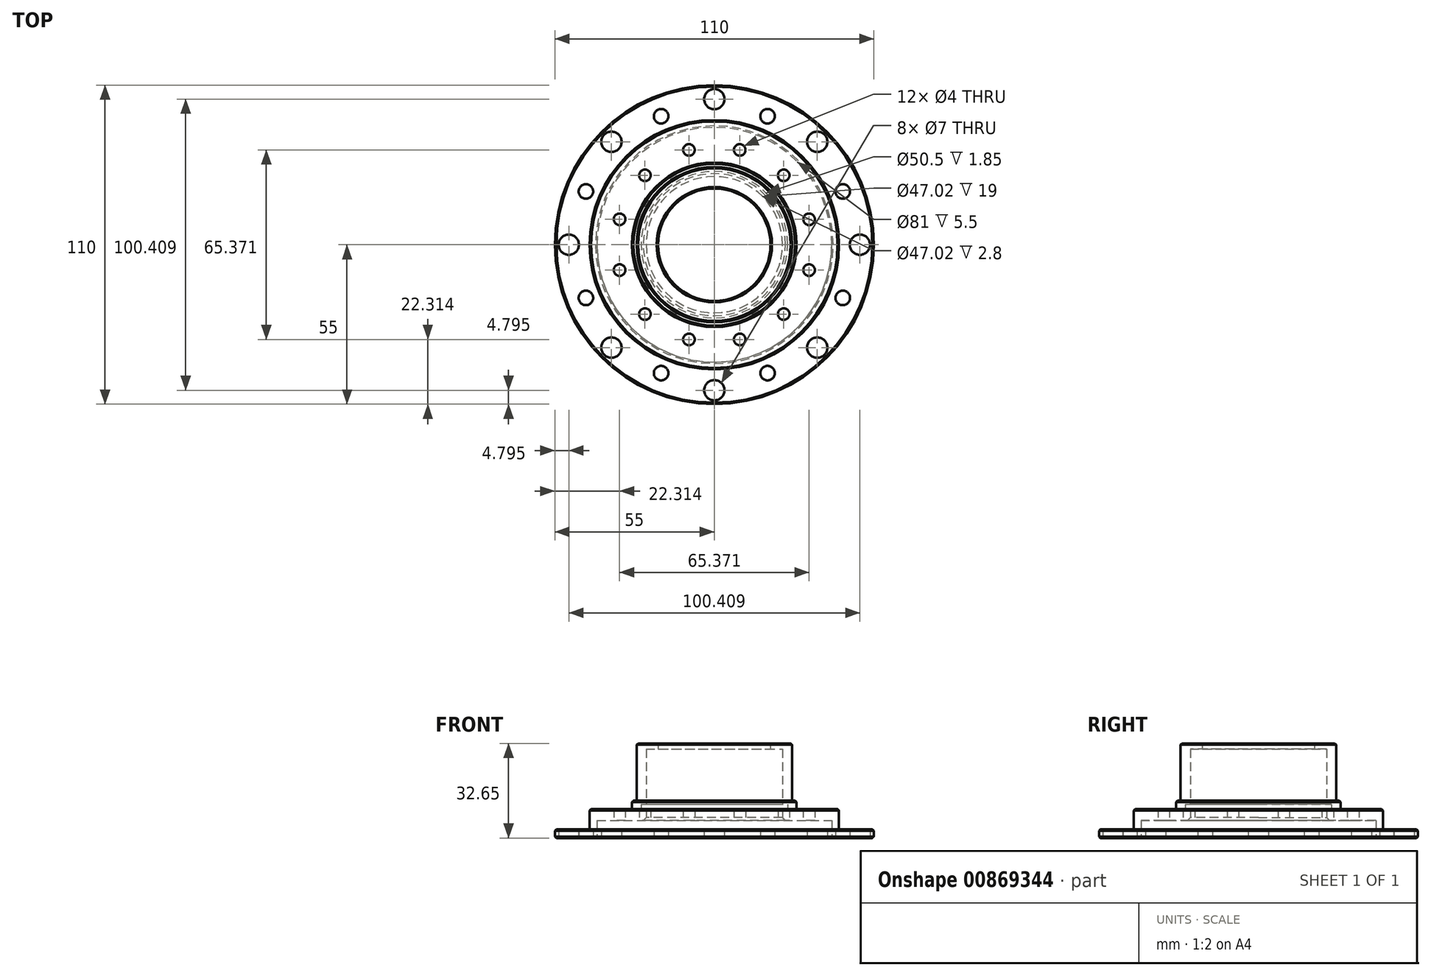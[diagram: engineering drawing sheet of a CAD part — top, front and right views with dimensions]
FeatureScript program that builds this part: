
annotation { "Feature Type Name" : "Feature", "Feature Type Description" : "" }
export const myFeature = defineFeature(function(context is Context, id is Id, definition is map)
    precondition{}
    {
        {
            var Q0;
            Q0=qCreatedBy(makeId("Front.planeOp"),FACE);
            var sketch = newSketch(context, id + "F0", { "sketchPlane" : qUnion([Q0])});
            skLineSegment(sketch, "E0", {"start": v(-40.5, 0) * mm, "end": v(-55, 0) * mm, "construction": true});
            skLineSegment(sketch, "E1", {"start": v(-55, 0) * mm, "end": v(-40.5, 0) * mm});
            skLineSegment(sketch, "E2", {"start": v(-40.5, 0) * mm, "end": v(-40.5, 6) * mm});
            skLineSegment(sketch, "E3", {"start": v(-55, 0) * mm, "end": v(-55, 3) * mm});
            skLineSegment(sketch, "E4", {"start": v(-55, 3) * mm, "end": v(-43, 3) * mm, "construction": true});
            skPoint(sketch, "E5", {"position": v(-43, 3) * mm});
            skLineSegment(sketch, "E6", {"start": v(-55, 3) * mm, "end": v(-43, 3) * mm});
            skLineSegment(sketch, "E7", {"start": v(-43, 3) * mm, "end": v(-43, 10) * mm});
            skLineSegment(sketch, "E8", {"start": v(-43, 10) * mm, "end": v(-28.39, 10) * mm});
            skPoint(sketch, "E9.orphan", {"position": v(0, 3) * mm});
            skPoint(sketch, "E10.orphan", {"position": v(0, 0) * mm});
            skPoint(sketch, "E11.end.orphan", {"position": v(0, 6) * mm});
            skPoint(sketch, "E11.start.orphan", {"position": v(0, 10) * mm});
            skLineSegment(sketch, "E12", {"start": v(-40.5, 6) * mm, "end": v(-23.51, 6) * mm});
            skLineSegment(sketch, "E13", {"start": v(-23.51, 9.8) * mm, "end": v(-25.25, 9.8) * mm});
            skLineSegment(sketch, "E14", {"start": v(-25.25, 9.8) * mm, "end": v(-25.25, 11.65) * mm});
            skLineSegment(sketch, "E15", {"start": v(-25.25, 11.65) * mm, "end": v(-23.51, 11.65) * mm});
            skLineSegment(sketch, "E16", {"start": v(-26.81, 12.92) * mm, "end": v(-26.81, 32.65) * mm});
            skLineSegment(sketch, "E17", {"start": v(-26.81, 32.65) * mm, "end": v(-19.38, 32.65) * mm});
            skLineSegment(sketch, "E18", {"start": v(-19.38, 32.65) * mm, "end": v(-19.38, 30.65) * mm});
            skLineSegment(sketch, "E19", {"start": v(-19.38, 30.65) * mm, "end": v(-23.51, 30.65) * mm});
            skLineSegment(sketch, "E20", {"start": v(-19.38, 30.65) * mm, "end": v(0, 30.65) * mm, "construction": true});
            skLineSegment(sketch, "E21", {"start": v(0, 30.65) * mm, "end": v(0, 32.65) * mm, "construction": true});
            skLineSegment(sketch, "E22", {"start": v(0, 32.65) * mm, "end": v(-19.38, 32.65) * mm, "construction": true});
            skLineSegment(sketch, "E23", {"start": v(-23.51, 9.8) * mm, "end": v(-23.51, 6) * mm});
            skLineSegment(sketch, "E24", {"start": v(-23.51, 11.65) * mm, "end": v(-23.51, 30.65) * mm});
            skLineSegment(sketch, "E25", {"start": v(-26.81, 12.92) * mm, "end": v(-28.39, 12.92) * mm});
            skLineSegment(sketch, "E26", {"start": v(-28.39, 12.92) * mm, "end": v(-28.39, 10) * mm});
            skPoint(sketch, "E27.orphan", {"position": v(-26.81, 10) * mm});
            skSolve(sketch);
        }
        {
            var Q0;
            Q0=makeQuery(id+"F0.imprint","IMPRINT",FACE,{"disambiguationData":[TD([[makeQuery(id+"F0.imprint","IMPRINT",EDGE,{"derivedFrom":sQuery(id+"F0.wireOp",EDGE,"E1")}),1.0]])]});
            var Q1;
            Q1=sQuery(id+"F0.wireOp",EDGE,"E21");
            revolve(context, id + "F1", {"surfaceOperationType" : NewSurfaceOperationType.NEW, "entities" : qUnion([Q0]), "axis" : qUnion([Q1]), "revolveType" : RevolveType.FULL});
        }
        {
            var Q0;
            Q0=qCreatedBy(makeId("Top.planeOp"),FACE);
            var sketch = newSketch(context, id + "F2", { "sketchPlane" : qUnion([Q0])});
            skCircle(sketch, "E28.cCircle", {"center": v(0, 0) * mm, "radius": 35.5 * mm, "construction": true});
            skLineSegment(sketch, "E28.0", {"start": v(35.5, -35.5) * mm, "end": v(-35.5, -35.5) * mm, "construction": true});
            skLineSegment(sketch, "E28.1", {"start": v(-35.5, -35.5) * mm, "end": v(-35.5, 35.5) * mm, "construction": true});
            skLineSegment(sketch, "E28.2", {"start": v(-35.5, 35.5) * mm, "end": v(35.5, 35.5) * mm, "construction": true});
            skLineSegment(sketch, "E28.3", {"start": v(35.5, 35.5) * mm, "end": v(35.5, -35.5) * mm, "construction": true});
            skPoint(sketch, "E28.0.midPoint", {"position": v(0, -35.5) * mm});
            skLineSegment(sketch, "E29", {"start": v(0, -23.44) * mm, "end": v(-1.5, -23.44) * mm});
            skLineSegment(sketch, "E30", {"start": v(1.5, -23.44) * mm, "end": v(0, -23.44) * mm});
            skLineSegment(sketch, "E31", {"start": v(-1.5, -23.44) * mm, "end": v(-1.5, -24.98) * mm});
            skLineSegment(sketch, "E32", {"start": v(-1.5, -24.98) * mm, "end": v(1.5, -24.98) * mm});
            skLineSegment(sketch, "E33", {"start": v(1.5, -24.98) * mm, "end": v(1.5, -23.44) * mm});
            skCircle(sketch, "E34.cCircle", {"center": v(0, 0) * mm, "radius": 44.3 * mm, "construction": true});
            skLineSegment(sketch, "E34.0", {"start": v(18.35, -44.3) * mm, "end": v(-18.35, -44.3) * mm, "construction": true});
            skLineSegment(sketch, "E34.1", {"start": v(-18.35, -44.3) * mm, "end": v(-44.3, -18.35) * mm, "construction": true});
            skLineSegment(sketch, "E34.2", {"start": v(-44.3, -18.35) * mm, "end": v(-44.3, 18.35) * mm, "construction": true});
            skLineSegment(sketch, "E34.3", {"start": v(-44.3, 18.35) * mm, "end": v(-18.35, 44.3) * mm, "construction": true});
            skLineSegment(sketch, "E34.4", {"start": v(-18.35, 44.3) * mm, "end": v(18.35, 44.3) * mm, "construction": true});
            skLineSegment(sketch, "E34.5", {"start": v(18.35, 44.3) * mm, "end": v(44.3, 18.35) * mm, "construction": true});
            skLineSegment(sketch, "E34.6", {"start": v(44.3, 18.35) * mm, "end": v(44.3, -18.35) * mm, "construction": true});
            skLineSegment(sketch, "E34.7", {"start": v(44.3, -18.35) * mm, "end": v(18.35, -44.3) * mm, "construction": true});
            skPoint(sketch, "E34.0.midPoint", {"position": v(0, -44.3) * mm});
            skLineSegment(sketch, "E35", {"start": v(0, 0) * mm, "end": v(-50.2, 0) * mm, "construction": true});
            skPoint(sketch, "E36", {"position": v(50.2, 0) * mm});
            skPoint(sketch, "E37", {"position": v(0, -50.2) * mm});
            skPoint(sketch, "E38", {"position": v(0, 50.2) * mm});
            skCircle(sketch, "E39.cCircle", {"center": v(0, 0) * mm, "radius": 32.69 * mm, "construction": true});
            skPoint(sketch, "E39.cCircle.perimeterSnap0", {"position": v(0, 35.5) * mm});
            skLineSegment(sketch, "E39.0", {"start": v(-8.76, 32.69) * mm, "end": v(8.76, 32.69) * mm, "construction": true});
            skLineSegment(sketch, "E39.1", {"start": v(8.76, 32.69) * mm, "end": v(23.93, 23.93) * mm, "construction": true});
            skLineSegment(sketch, "E39.2", {"start": v(23.93, 23.93) * mm, "end": v(32.69, 8.76) * mm, "construction": true});
            skLineSegment(sketch, "E39.3", {"start": v(32.69, 8.76) * mm, "end": v(32.69, -8.76) * mm, "construction": true});
            skLineSegment(sketch, "E39.4", {"start": v(32.69, -8.76) * mm, "end": v(23.93, -23.93) * mm, "construction": true});
            skLineSegment(sketch, "E39.5", {"start": v(23.93, -23.93) * mm, "end": v(8.76, -32.69) * mm, "construction": true});
            skLineSegment(sketch, "E39.6", {"start": v(8.76, -32.69) * mm, "end": v(-8.76, -32.69) * mm, "construction": true});
            skLineSegment(sketch, "E39.7", {"start": v(-8.76, -32.69) * mm, "end": v(-23.93, -23.93) * mm, "construction": true});
            skLineSegment(sketch, "E39.8", {"start": v(-23.93, -23.93) * mm, "end": v(-32.69, -8.76) * mm, "construction": true});
            skLineSegment(sketch, "E39.9", {"start": v(-32.69, -8.76) * mm, "end": v(-32.69, 8.76) * mm, "construction": true});
            skLineSegment(sketch, "E39.10", {"start": v(-32.69, 8.76) * mm, "end": v(-23.93, 23.93) * mm, "construction": true});
            skLineSegment(sketch, "E39.11", {"start": v(-23.93, 23.93) * mm, "end": v(-8.76, 32.69) * mm, "construction": true});
            skPoint(sketch, "E39.0.midPoint", {"position": v(0, 32.69) * mm});
            skPoint(sketch, "E39.0.midPoint.positionSnap0", {"position": v(0, 35.5) * mm});
            skSolve(sketch);
        }
        {
            var Q0;
            Q0=sQuery(id+"F2.wireOp",VERTEX,"E28.0.end");
            var Q1;
            Q1=sQuery(id+"F2.wireOp",VERTEX,"E28.0.start");
            var Q2;
            Q2=sQuery(id+"F2.wireOp",VERTEX,"E28.2.end");
            var Q3;
            Q3=sQuery(id+"F2.wireOp",VERTEX,"E28.1.end");
            var Q4;
            Q4=makeQuery(id+"F1.opRevolve","SWEPT_BODY",BODY,{"disambiguationData":[OSD([sQuery(id+"F0.wireOp",EDGE,"E1"),sQuery(id+"F0.wireOp",EDGE,"E2"),sQuery(id+"F0.wireOp",EDGE,"E3"),sQuery(id+"F0.wireOp",EDGE,"E6"),sQuery(id+"F0.wireOp",EDGE,"E7"),sQuery(id+"F0.wireOp",EDGE,"E8"),sQuery(id+"F0.wireOp",EDGE,"E12"),sQuery(id+"F0.wireOp",EDGE,"MZGkjb6Y-36Ue-xZFx-bMgy-8CVt9Qpu78Rd"),sQuery(id+"F0.wireOp",EDGE,"E13"),sQuery(id+"F0.wireOp",EDGE,"E14"),sQuery(id+"F0.wireOp",EDGE,"E15"),sQuery(id+"F0.wireOp",EDGE,"rAh7Tcj1-8SW7-fxsf-8VIu-JH5fEd8qC4TA"),sQuery(id+"F0.wireOp",EDGE,"E16"),sQuery(id+"F0.wireOp",EDGE,"E17"),sQuery(id+"F0.wireOp",EDGE,"E18"),sQuery(id+"F0.wireOp",EDGE,"E19")])]});
            hole(context, id + "F3", {"style" : HoleStyle.SIMPLE, "endStyle" : HoleEndStyle.THROUGH, "oppositeDirection" : true, "holeDiameter" : 7 * mm, "majorDiameter" : 5 * mm, "isTappedThrough" : true, "tappedDepth" : 12.7 * mm, "tapClearance" : 3, "startFromSketch" : true, "locations" : qUnion([Q0, Q1, Q2, Q3]), "scope" : qUnion([Q4])});
        }
        {
            var Q0;
            Q0=sQuery(id+"F2.wireOp",VERTEX,"E34.0.end");
            var Q1;
            Q1=sQuery(id+"F2.wireOp",VERTEX,"E34.0.start");
            var Q2;
            Q2=sQuery(id+"F2.wireOp",VERTEX,"E34.6.end");
            var Q3;
            Q3=sQuery(id+"F2.wireOp",VERTEX,"E34.5.end");
            var Q4;
            Q4=sQuery(id+"F2.wireOp",VERTEX,"E34.4.end");
            var Q5;
            Q5=sQuery(id+"F2.wireOp",VERTEX,"E34.3.end");
            var Q6;
            Q6=sQuery(id+"F2.wireOp",VERTEX,"E34.2.end");
            var Q7;
            Q7=sQuery(id+"F2.wireOp",VERTEX,"E34.1.end");
            var Q8;
            Q8=makeQuery(id+"F1.opRevolve","SWEPT_BODY",BODY,{"disambiguationData":[OSD([sQuery(id+"F0.wireOp",EDGE,"E1"),sQuery(id+"F0.wireOp",EDGE,"E2"),sQuery(id+"F0.wireOp",EDGE,"E3"),sQuery(id+"F0.wireOp",EDGE,"E6"),sQuery(id+"F0.wireOp",EDGE,"E7"),sQuery(id+"F0.wireOp",EDGE,"E8"),sQuery(id+"F0.wireOp",EDGE,"E12"),sQuery(id+"F0.wireOp",EDGE,"MZGkjb6Y-36Ue-xZFx-bMgy-8CVt9Qpu78Rd"),sQuery(id+"F0.wireOp",EDGE,"E13"),sQuery(id+"F0.wireOp",EDGE,"E14"),sQuery(id+"F0.wireOp",EDGE,"E15"),sQuery(id+"F0.wireOp",EDGE,"rAh7Tcj1-8SW7-fxsf-8VIu-JH5fEd8qC4TA"),sQuery(id+"F0.wireOp",EDGE,"E16"),sQuery(id+"F0.wireOp",EDGE,"E17"),sQuery(id+"F0.wireOp",EDGE,"E18"),sQuery(id+"F0.wireOp",EDGE,"E19")])]});
            hole(context, id + "F4", {"style" : HoleStyle.SIMPLE, "endStyle" : HoleEndStyle.THROUGH, "oppositeDirection" : true, "holeDiameter" : 5 * mm, "majorDiameter" : 5 * mm, "isTappedThrough" : true, "tappedDepth" : 12.7 * mm, "tapClearance" : 3, "startFromSketch" : true, "locations" : qUnion([Q0, Q1, Q2, Q3, Q4, Q5, Q6, Q7]), "scope" : qUnion([Q8])});
        }
        {
            var Q0;
            Q0=sQuery(id+"F2.wireOp",VERTEX,"E37");
            var Q1;
            Q1=sQuery(id+"F2.wireOp",VERTEX,"E35.end");
            var Q2;
            Q2=sQuery(id+"F2.wireOp",VERTEX,"E36");
            var Q3;
            Q3=sQuery(id+"F2.wireOp",VERTEX,"E38");
            var Q4;
            Q4=makeQuery(id+"F1.opRevolve","SWEPT_BODY",BODY,{"disambiguationData":[OSD([sQuery(id+"F0.wireOp",EDGE,"E1"),sQuery(id+"F0.wireOp",EDGE,"E2"),sQuery(id+"F0.wireOp",EDGE,"E3"),sQuery(id+"F0.wireOp",EDGE,"E6"),sQuery(id+"F0.wireOp",EDGE,"E7"),sQuery(id+"F0.wireOp",EDGE,"E8"),sQuery(id+"F0.wireOp",EDGE,"E12"),sQuery(id+"F0.wireOp",EDGE,"MZGkjb6Y-36Ue-xZFx-bMgy-8CVt9Qpu78Rd"),sQuery(id+"F0.wireOp",EDGE,"E13"),sQuery(id+"F0.wireOp",EDGE,"E14"),sQuery(id+"F0.wireOp",EDGE,"E15"),sQuery(id+"F0.wireOp",EDGE,"rAh7Tcj1-8SW7-fxsf-8VIu-JH5fEd8qC4TA"),sQuery(id+"F0.wireOp",EDGE,"E16"),sQuery(id+"F0.wireOp",EDGE,"E17"),sQuery(id+"F0.wireOp",EDGE,"E18"),sQuery(id+"F0.wireOp",EDGE,"E19")])]});
            hole(context, id + "F5", {"style" : HoleStyle.SIMPLE, "endStyle" : HoleEndStyle.THROUGH, "oppositeDirection" : true, "holeDiameter" : 7 * mm, "majorDiameter" : 5 * mm, "isTappedThrough" : true, "tappedDepth" : 12.7 * mm, "tapClearance" : 3, "startFromSketch" : true, "locations" : qUnion([Q0, Q1, Q2, Q3]), "scope" : qUnion([Q4])});
        }
        {
            var Q0;
            Q0=sQuery(id+"F2.wireOp",VERTEX,"E39.10.end");
            var Q1;
            Q1=sQuery(id+"F2.wireOp",VERTEX,"E39.0.start");
            var Q2;
            Q2=sQuery(id+"F2.wireOp",VERTEX,"E39.0.end");
            var Q3;
            Q3=sQuery(id+"F2.wireOp",VERTEX,"E39.1.end");
            var Q4;
            Q4=sQuery(id+"F2.wireOp",VERTEX,"E39.2.end");
            var Q5;
            Q5=sQuery(id+"F2.wireOp",VERTEX,"E39.3.end");
            var Q6;
            Q6=sQuery(id+"F2.wireOp",VERTEX,"E39.4.end");
            var Q7;
            Q7=sQuery(id+"F2.wireOp",VERTEX,"E39.5.end");
            var Q8;
            Q8=sQuery(id+"F2.wireOp",VERTEX,"E39.6.end");
            var Q9;
            Q9=sQuery(id+"F2.wireOp",VERTEX,"E39.7.end");
            var Q10;
            Q10=sQuery(id+"F2.wireOp",VERTEX,"E39.8.end");
            var Q11;
            Q11=sQuery(id+"F2.wireOp",VERTEX,"E39.9.end");
            var Q12;
            Q12=makeQuery(id+"F1.opRevolve","SWEPT_BODY",BODY,{"disambiguationData":[OSD([sQuery(id+"F0.wireOp",EDGE,"E1"),sQuery(id+"F0.wireOp",EDGE,"E2"),sQuery(id+"F0.wireOp",EDGE,"E3"),sQuery(id+"F0.wireOp",EDGE,"E6"),sQuery(id+"F0.wireOp",EDGE,"E7"),sQuery(id+"F0.wireOp",EDGE,"E8"),sQuery(id+"F0.wireOp",EDGE,"E12"),sQuery(id+"F0.wireOp",EDGE,"MZGkjb6Y-36Ue-xZFx-bMgy-8CVt9Qpu78Rd"),sQuery(id+"F0.wireOp",EDGE,"E13"),sQuery(id+"F0.wireOp",EDGE,"E14"),sQuery(id+"F0.wireOp",EDGE,"E15"),sQuery(id+"F0.wireOp",EDGE,"rAh7Tcj1-8SW7-fxsf-8VIu-JH5fEd8qC4TA"),sQuery(id+"F0.wireOp",EDGE,"E16"),sQuery(id+"F0.wireOp",EDGE,"E17"),sQuery(id+"F0.wireOp",EDGE,"E18"),sQuery(id+"F0.wireOp",EDGE,"E19")])]});
            hole(context, id + "F6", {"style" : HoleStyle.SIMPLE, "endStyle" : HoleEndStyle.THROUGH, "oppositeDirection" : true, "holeDiameter" : 4 * mm, "majorDiameter" : 5 * mm, "isTappedThrough" : true, "tappedDepth" : 12.7 * mm, "tapClearance" : 3, "startFromSketch" : true, "locations" : qUnion([Q0, Q1, Q2, Q3, Q4, Q5, Q6, Q7, Q8, Q9, Q10, Q11]), "scope" : qUnion([Q12])});
        }
        {
            var Q0;
            Q0=makeQuery(id+"F1.opRevolve","SWEPT_EDGE",EDGE,{"disambiguationData":[OSD([sQuery(id+"F0.wireOp",EDGE,"E12"),sQuery(id+"F0.wireOp",EDGE,"E23")])]});
            chamfer(context, id + "F7", {"entities" : qUnion([Q0]), "width" : 1 * mm, "tangentPropagation" : true});
        }
        {
            var Q0;
            Q0=makeQuery(id+"F1.opRevolve","SWEPT_EDGE",EDGE,{"disambiguationData":[OSD([sQuery(id+"F0.wireOp",EDGE,"E3"),sQuery(id+"F0.wireOp",EDGE,"E6")])]});
            var Q1;
            Q1=makeQuery(id+"F1.opRevolve","SWEPT_EDGE",EDGE,{"disambiguationData":[OSD([sQuery(id+"F0.wireOp",EDGE,"E7"),sQuery(id+"F0.wireOp",EDGE,"E8")])]});
            var Q2;
            Q2=makeQuery(id+"F1.opRevolve","SWEPT_EDGE",EDGE,{"disambiguationData":[OSD([sQuery(id+"F0.wireOp",EDGE,"E25"),sQuery(id+"F0.wireOp",EDGE,"E26")])]});
            var Q3;
            Q3=makeQuery(id+"F1.opRevolve","SWEPT_EDGE",EDGE,{"disambiguationData":[OSD([sQuery(id+"F0.wireOp",EDGE,"E16"),sQuery(id+"F0.wireOp",EDGE,"E17")])]});
            chamfer(context, id + "F8", {"entities" : qUnion([Q0, Q1, Q2, Q3]), "width" : 0.5 * mm, "tangentPropagation" : true});
        }
        {
            var Q0;
            Q0=makeQuery(id+"F1.opRevolve","SWEPT_EDGE",EDGE,{"disambiguationData":[OSD([sQuery(id+"F0.wireOp",EDGE,"E1"),sQuery(id+"F0.wireOp",EDGE,"E2")])]});
            chamfer(context, id + "F9", {"entities" : qUnion([Q0]), "width" : 0.5 * mm, "tangentPropagation" : true});
        }
        {
            var Q0;
            Q0=makeQuery(id+"F1.opRevolve","SWEPT_EDGE",EDGE,{"disambiguationData":[OSD([sQuery(id+"F0.wireOp",EDGE,"E1"),sQuery(id+"F0.wireOp",EDGE,"E3")])]});
            chamfer(context, id + "F10", {"entities" : qUnion([Q0]), "width" : 0.5 * mm, "tangentPropagation" : true});
        }
        {
            var Q0;
            Q0=makeQuery(id+"F1.opRevolve","SWEPT_EDGE",EDGE,{"disambiguationData":[OSD([sQuery(id+"F0.wireOp",EDGE,"E17"),sQuery(id+"F0.wireOp",EDGE,"E18")])]});
            chamfer(context, id + "F11", {"entities" : qUnion([Q0]), "width" : 0.5 * mm, "tangentPropagation" : true});
        }
    });
